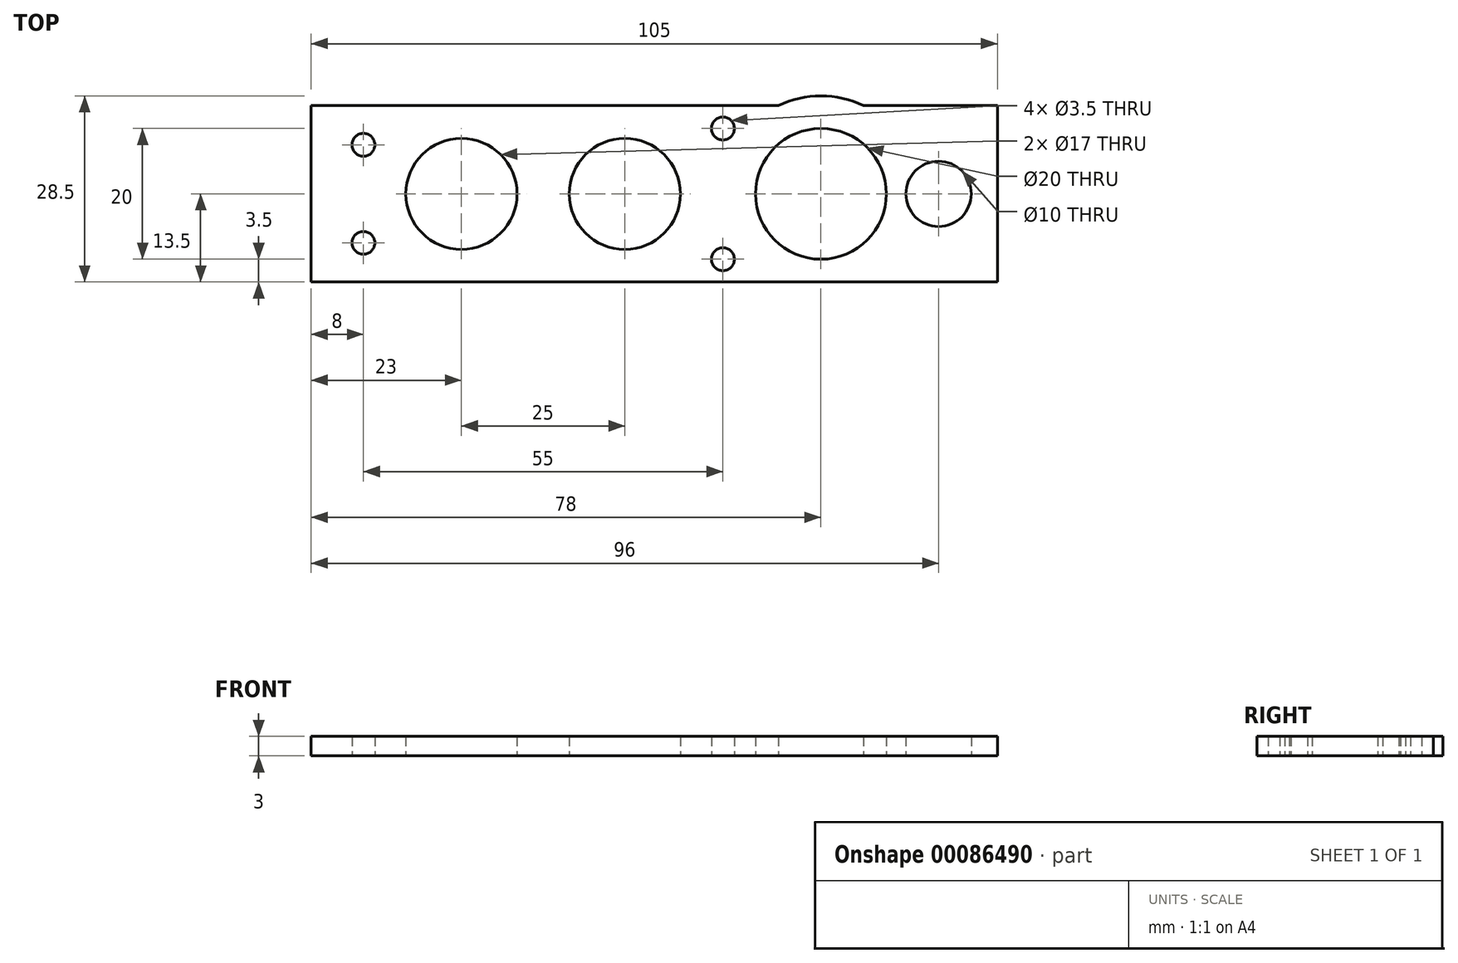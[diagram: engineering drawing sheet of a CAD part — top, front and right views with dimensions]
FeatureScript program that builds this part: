
annotation { "Feature Type Name" : "Feature", "Feature Type Description" : "" }
export const myFeature = defineFeature(function(context is Context, id is Id, definition is map)
    precondition{}
    {
        {
            var Q0;
            Q0=qCreatedBy(makeId("Top.planeOp"),FACE);
            var sketch = newSketch(context, id + "F0", { "sketchPlane" : qUnion([Q0])});
            skPoint(sketch, "E0", {"position": v(-55, 7.5) * mm});
            skPoint(sketch, "E1", {"position": v(0, 10) * mm});
            skLineSegment(sketch, "E2.bottom", {"start": v(42, 13.5) * mm, "end": v(-63, 13.5) * mm});
            skLineSegment(sketch, "E2.top", {"start": v(42, -13.5) * mm, "end": v(-63, -13.5) * mm});
            skLineSegment(sketch, "E2.left", {"start": v(42, 13.5) * mm, "end": v(42, -13.5) * mm});
            skLineSegment(sketch, "E2.right", {"start": v(-63, 13.5) * mm, "end": v(-63, -13.5) * mm});
            skPoint(sketch, "E2.middle", {"position": v(-10.5, 0) * mm});
            skCircle(sketch, "E3", {"center": v(-55, 7.5) * mm, "radius": 1.75 * mm});
            skCircle(sketch, "E4", {"center": v(0, 10) * mm, "radius": 1.75 * mm});
            skCircle(sketch, "E5.MirrorC", {"center": v(-55, -7.5) * mm, "radius": 1.75 * mm});
            skCircle(sketch, "E6.MirrorC", {"center": v(0, -10) * mm, "radius": 1.75 * mm});
            skCircle(sketch, "E7", {"center": v(-40, 0) * mm, "radius": 8.5 * mm});
            skCircle(sketch, "E8", {"center": v(-15, 0) * mm, "radius": 8.5 * mm});
            skLineSegment(sketch, "E9.bottom", {"start": v(42, 13.5) * mm, "end": v(36, 13.5) * mm});
            skLineSegment(sketch, "E9.top", {"start": v(42, 19.5) * mm, "end": v(36, 19.5) * mm});
            skLineSegment(sketch, "E9.left", {"start": v(42, 13.5) * mm, "end": v(42, 19.5) * mm});
            skLineSegment(sketch, "E9.right", {"start": v(36, 13.5) * mm, "end": v(36, 19.5) * mm});
            skLineSegment(sketch, "E10.MirrorCS", {"start": v(42, -13.5) * mm, "end": v(36, -13.5) * mm});
            skLineSegment(sketch, "E11.MirrorCS", {"start": v(42, -13.5) * mm, "end": v(42, -19.5) * mm});
            skLineSegment(sketch, "E12.MirrorCS", {"start": v(42, -19.5) * mm, "end": v(36, -19.5) * mm});
            skLineSegment(sketch, "E13.MirrorCS", {"start": v(36, -13.5) * mm, "end": v(36, -19.5) * mm});
            skCircle(sketch, "E14", {"center": v(15, 0) * mm, "radius": 10 * mm});
            skCircle(sketch, "E15", {"center": v(33, 0) * mm, "radius": 5 * mm});
            skArc(sketch, "E16", {"start": v(21.54, -13.5) * mm, "mid": v(15, -15) * mm, "end": v(8.46, -13.5) * mm});
            skArc(sketch, "E17.MirrorCS", {"start": v(21.54, 13.5) * mm, "mid": v(15, 15) * mm, "end": v(8.46, 13.5) * mm});
            skSolve(sketch);
        }
        {
            var Q0;
            Q0=makeQuery(id+"F0.imprint","IMPRINT",FACE,{"disambiguationData":[TD([[makeQuery(id+"F0.imprint","IMPRINT",EDGE,{"derivedFrom":sQuery(id+"F0.wireOp",EDGE,"E2.bottom")}),1.0]])]});
            var Q1;
            Q1=makeQuery(id+"F0.imprint","IMPRINT",FACE,{"disambiguationData":[TD([[makeQuery(id+"F0.imprint","IMPRINT",EDGE,{"derivedFrom":sQuery(id+"F0.wireOp",EDGE,"E10.MirrorCS")}),1.0]])]});
            var Q2;
            Q2=makeQuery(id+"F0.imprint","IMPRINT",FACE,{"disambiguationData":[TD([[makeQuery(id+"F0.imprint","IMPRINT",EDGE,{"derivedFrom":sQuery(id+"F0.wireOp",EDGE,"E9.bottom")}),-1.0]])]});
            var Q3;
            {var subQ0=sQuery(id+"F0.wireOp",EDGE,"E17.MirrorCS");Q3=makeQuery(id+"F0.imprint","IMPRINT",FACE,{"disambiguationData":[TD([[makeQuery(id+"F0.imprint","IMPRINT",EDGE,{"derivedFrom":subQ0}),1.0]])]});}
            var Q4;
            {var subQ0=sQuery(id+"F0.wireOp",EDGE,"E16");Q4=makeQuery(id+"F0.imprint","IMPRINT",FACE,{"disambiguationData":[TD([[makeQuery(id+"F0.imprint","IMPRINT",EDGE,{"derivedFrom":subQ0}),-1.0]])]});}
            extrude(context, id + "F1", {"entities" : qUnion([Q0, Q1, Q2, Q3, Q4]), "depth" : 3 * mm});
        }
    });
